# Revit family: Verano_V790_Solano_GM_R21
name_source: partatom
category: Generic Models
units: mm (PartAtom-declared; Revit-internal decimal feet)

## family parameters
Always vertical = Yes
Can host rebar = No
Cut with Voids When Loaded = No
Part Type = Normal
Room Calculation Point = No
Round Connector Dimension = Use Diameter
Shared = No
Work Plane-Based = No

## types (2) — shared parameters
Description = The Solano sliding glass doors are a classic model. The completely aluminium framework will give ‘body’ to the glass work and provide a wind and watertight partition. The Solano’s hinges and locks will ensure your garden furniture and accessories will be secure when you are not at home.
Manufacturer = Verano Systems
Maximal Height = 2600 mm  [stored 8.53018 ft]
Maximal Width 2 Part = 3500 mm  [stored 11.4829 ft]
Maximal Width 4 Part = 6000 mm  [stored 19.685 ft]
Minimal Height = 2000 mm  [stored 6.56168 ft]
Minimal Width 2 Part = 1500 mm  [stored 4.92126 ft]
Minimal Width 4 Part = 3500 mm  [stored 11.4829 ft]
Model = V790 Solano
Panel End Stop = 41 mm  [stored 0.134514 ft]
Panel Offset = 22 mm  [stored 0.0721785 ft]
URL = https://verano.nl
zero-valued in all types: Default Elevation

## per-type parameters (varying)
| type | 2 Part | 4 Part |
| 2 Part | Yes | No |
| 4 Part | No | Yes |

note: [stored X ft] marks values corroborated as IEEE doubles in the binary element streams (Revit-internal decimal feet)

## geometry (parser evidence)
native form markers: Sweep x16
no freeform markers — native parametric forms only
